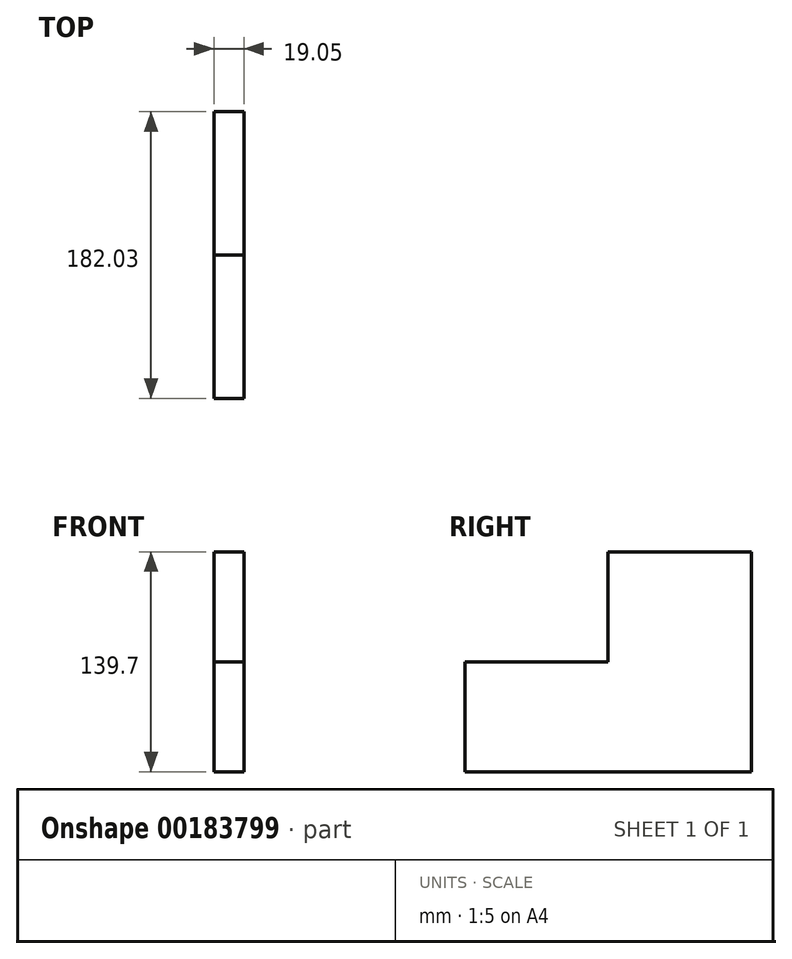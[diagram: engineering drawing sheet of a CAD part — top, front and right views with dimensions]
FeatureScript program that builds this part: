
annotation { "Feature Type Name" : "Feature", "Feature Type Description" : "" }
export const myFeature = defineFeature(function(context is Context, id is Id, definition is map)
    precondition{}
    {
        {
            var Q0;
            Q0=qCreatedBy(makeId("Right.planeOp"),FACE);
            var sketch = newSketch(context, id + "F0", { "sketchPlane" : qUnion([Q0])});
            skLineSegment(sketch, "E0.bottom", {"start": v(0, 0) * mm, "end": v(273.05, 0) * mm});
            skLineSegment(sketch, "E0.top", {"start": v(0, 228.6) * mm, "end": v(273.05, 228.6) * mm});
            skLineSegment(sketch, "E0.left", {"start": v(0, 0) * mm, "end": v(0, 228.6) * mm});
            skLineSegment(sketch, "E0.right", {"start": v(273.05, 0) * mm, "end": v(273.05, 228.6) * mm});
            skSolve(sketch);
        }
        {
            var Q0;
            Q0=qSketchRegion(id+"F0",true);
            extrude(context, id + "F1", {"entities" : qUnion([Q0]), "oppositeDirection" : true, "depth" : 19.05 * mm});
        }
        {
            var Q0;
            Q0=makeQuery(id+"F1.opExtrude","CAP_FACE",FACE,{"disambiguationData":[OSD([sQuery(id+"F0.wireOp",EDGE,"E0.bottom"),sQuery(id+"F0.wireOp",EDGE,"E0.top"),sQuery(id+"F0.wireOp",EDGE,"E0.left"),sQuery(id+"F0.wireOp",EDGE,"E0.right")])],"isStart":true});
            var sketch = newSketch(context, id + "F2", { "sketchPlane" : qUnion([Q0])});
            skLineSegment(sketch, "E1", {"start": v(91.02, 228.6) * mm, "end": v(91.02, 69.85) * mm, "construction": true});
            skLineSegment(sketch, "E2", {"start": v(182.03, 228.6) * mm, "end": v(182.03, 139.7) * mm, "construction": true});
            skLineSegment(sketch, "E3", {"start": v(0, 190.24) * mm, "end": v(91.02, 190.24) * mm, "construction": true});
            skLineSegment(sketch, "E4", {"start": v(91.02, 190.24) * mm, "end": v(182.03, 190.24) * mm, "construction": true});
            skLineSegment(sketch, "E5", {"start": v(182.03, 190.24) * mm, "end": v(273.05, 190.24) * mm, "construction": true});
            skLineSegment(sketch, "E6", {"start": v(273.05, 139.7) * mm, "end": v(182.03, 139.7) * mm});
            skLineSegment(sketch, "E7", {"start": v(273.05, 69.85) * mm, "end": v(91.02, 69.85) * mm});
            skLineSegment(sketch, "E8", {"start": v(40.37, 139.7) * mm, "end": v(40.37, 69.85) * mm, "construction": true});
            skLineSegment(sketch, "E9", {"start": v(40.37, 69.85) * mm, "end": v(40.37, 0) * mm, "construction": true});
            skLineSegment(sketch, "E10", {"start": v(91.02, 69.85) * mm, "end": v(91.02, 0) * mm});
            skLineSegment(sketch, "E11", {"start": v(91.02, 69.85) * mm, "end": v(0, 69.85) * mm, "construction": true});
            skLineSegment(sketch, "E12", {"start": v(182.03, 139.7) * mm, "end": v(182.03, 0) * mm});
            skLineSegment(sketch, "E13", {"start": v(182.03, 139.7) * mm, "end": v(0, 139.7) * mm, "construction": true});
            skSolve(sketch);
        }
        {
            var Q0;
            {var subQ1=sQuery(id+"F2.wireOp",EDGE,"E6");Q0=makeQuery(id+"F2.imprint","IMPRINT",FACE,{"disambiguationData":[TD([[makeQuery(id+"F2.imprint","IMPRINT",EDGE,{"derivedFrom":subQ1}),-1.0]])]});}
            var Q1;
            Q1=makeQuery(id+"F1.opExtrude","CAP_FACE",FACE,{"disambiguationData":[OSD([sQuery(id+"F0.wireOp",EDGE,"E0.bottom"),sQuery(id+"F0.wireOp",EDGE,"E0.top"),sQuery(id+"F0.wireOp",EDGE,"E0.left"),sQuery(id+"F0.wireOp",EDGE,"E0.right")])],"isStart":false});
            extrude(context, id + "F3", {"entities" : qUnion([Q0]), "operationType" : NewBodyOperationType.REMOVE, "endBound" : BoundingType.UP_TO_SURFACE, "oppositeDirection" : true, "endBoundEntityFace" : qUnion([Q1]), "depth" : 25.4 * mm});
        }
    });
